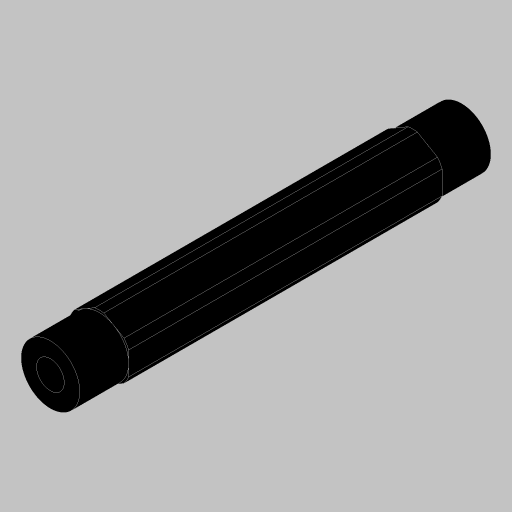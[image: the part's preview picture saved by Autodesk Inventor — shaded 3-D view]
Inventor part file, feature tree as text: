
AUTODESK INVENTOR PART (.ipt)
format: ipt  version: 2023.5 (Build 275446000, 446)  size: 176,128 bytes
history: native  units: in
note: dims shown in document units (in); Inventor stores cm internally (conversion verified against a paired STEP export)
features: extrude x3, projected_geometry x3, hole x1, mirror x1, sketch x1
ambient origin geometry x8: Origin, YZ Plane, XZ Plane, XY Plane, X Axis, Y Axis, Z Axis, Center Point
bodies: Solid1 (feature_tree)
feature tree (9):
  extrude  "Extrusion1"  Depth=0.375in
  hole  "Hole1"  [1 undecoded]
  extrude  "Extrusion3"  Depth=0.312in TaperAngle=0.0deg
  extrude  "Extrusion4"  Depth=0.375in
  mirror  "Mirror2"
  sketch  "Sketch5"  dims[d2=0.0in d9=0.625in d10=0.385in d11=0.25in d12=0.5635in d13=1.0in d14=0.8108in d16=0.7in d17=0.0in d18=0.0in d19=0.312in d20=0.0in d21=0.375in d22=0.5in d23=0.0344in d24=0.5in d25=0.0344in]
  projected_geometry  "Projected Loop2"
  projected_geometry  "Project Cut Edges1"
  projected_geometry  "Project Cut Edges2"
note: 1 required parameter value undecoded (feature->parameter linkage not recoverable at this tier; creation-order binding heuristic only, values carry confidence <= 0.55)
